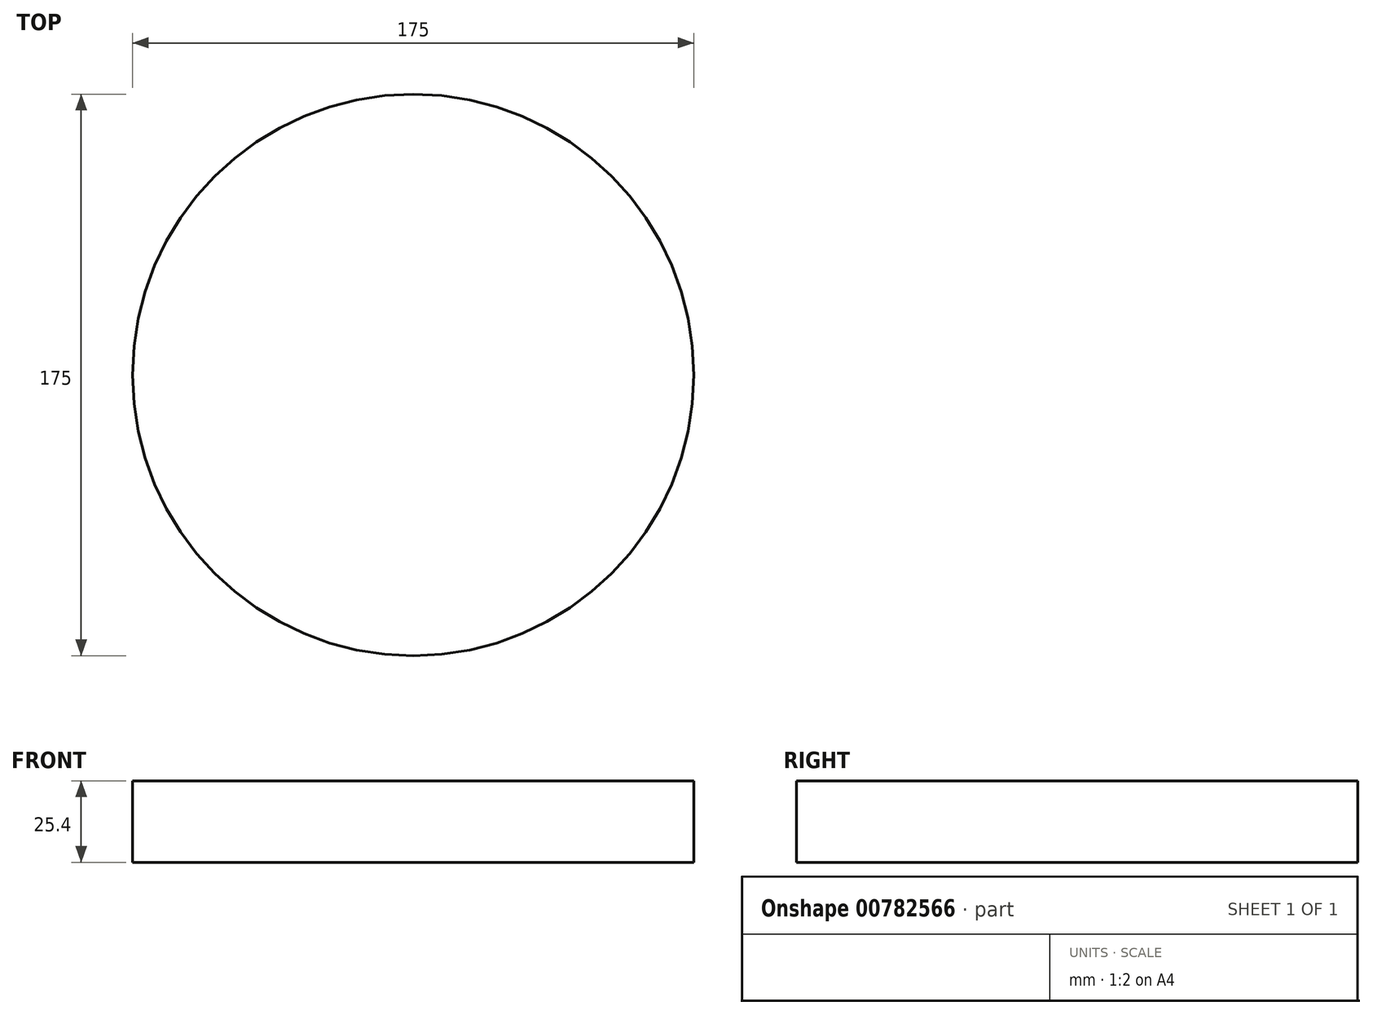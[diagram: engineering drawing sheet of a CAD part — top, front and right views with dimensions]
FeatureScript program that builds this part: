
annotation { "Feature Type Name" : "Feature", "Feature Type Description" : "" }
export const myFeature = defineFeature(function(context is Context, id is Id, definition is map)
    precondition{}
    {
        {
            var Q0;
            Q0=qCreatedBy(makeId("Top.planeOp"),FACE);
            var sketch = newSketch(context, id + "F0", { "sketchPlane" : qUnion([Q0])});
            skCircle(sketch, "E0", {"center": v(0, 0) * mm, "radius": 87.5 * mm});
            skSolve(sketch);
        }
        {
            var Q0;
            Q0 = qSketchRegion(id + "F0", true);
            extrude(context, id + "F1", {"entities" : qUnion([Q0]), "depth" : 25.4 * mm, "offsetDistance" : 25.4 * mm});
        }
    });
